# Revit family: 1010212_GHR
name_source: partatom
category: Air Terminals
revit_build: Autodesk Revit MEP 2012 (Build: 20110309_2315(x64)
units: mm (PartAtom-declared; Revit-internal decimal feet)

## types (1)
- GHR
    Conect_Horizontal = 23 3/4"
    Conect_Vertical = 23 3/4"
    Cuello Cuadrado Min-Max = 4"x4" a 24"x24" Incrementos de 1"
    Cuello Rectangular Min-Max = 5"x4" a 48"x24" Incrementos de 1"
    Deflexion = Fijo a 45°
    Description = Rejilla de extracción o retorno tipo panal
    Funcion = Extracción/Retorno
    Horizontal = 24"
    Manufacturer = INNES
    Material = Aluminio/Acero/Inoxidable
    Medida_Requerida_Horizontal = 24"
    Medida_Requerida_Vertical = 24"
    Model = GHR
    Nota1 = .
    Posicion de Instalacion = Muro
    Tipo de Cuello = Cuadrado/Rectangular
    Type Comments = Marco extruido
    URL = https://www.innes.com.mx
    Vertical = 24"
    Visible_Texto = No

## geometry (parser evidence)
native form markers: Sweep x9
no freeform markers — native parametric forms only
